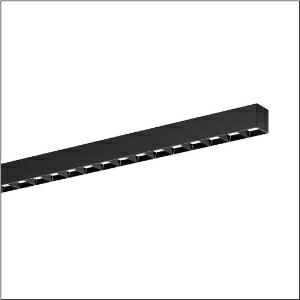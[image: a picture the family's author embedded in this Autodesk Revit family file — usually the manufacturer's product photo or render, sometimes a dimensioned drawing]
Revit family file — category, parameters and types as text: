
# Revit family: silica_21_51mx21dc3abb
name_source: partatom
category: Lighting Fixtures
units: mm (PartAtom-declared; Revit-internal decimal feet)

## family parameters
Cut with Voids When Loaded = No
Host = Face
Light Source = No
Part Type = Normal
Room Calculation Point = No
Round Connector Dimension = Use Diameter
Shared = No

## types (1)
- --- (1 x LED, 10800 lm, 69.3 W, 3000K)
    Apparent Load = 69 VA
    CIE Flux Codes = 87 99 100 100 100
    Color Rendering = 80
    Color Temperature = 3000K
    Default Elevation = 1800 mm
    Description = Silica 21, office luminaire, primary light control with darklight reflector, of PMMA, black, CAT 2 (L<= 3000cd/m²), light emission: direct distribution, primary light characteristic: symmetric, installation type: surface-mounted, LED, rated luminous flux: 10.800lm, luminous efficacy: 156lm/W, light colour: 830, colour temperature: 3000K, control gear: DALI 2, with terminal, 3+2-pole, max. 2.5mm², mains connection: 220..240V, AC, 50/60Hz, luminaire housing, of aluminium, matt jet black (RAL 9005), length: 3.004mm, width: 53mm, height: 53mm, protection rating (complete): IP20, insulation class (complete): insulation class I (protective earthing), certification: CE, permissible operating ambient temperature: 0..+35°C, standard: EN 50419, packaging unit: 1 piece
    Height = 53 mm
    Lamp = 1 x LED
    Lamp Light Flux = 10800 lm
    Lamp Power = 69.3 W
    Lamp count = 1
    Length = 3004 mm
    Luminous efficacy = 156 lm/W
    Manufacturer = Siteco
    ModVariant = No
    Model = 51MX21DC3ABB
    Mounting Place = Ceiling
    Mounting Type = Surface mounted
    Number of Poles = 1
    OnlyDefault = Yes
    Power Factor = 1
    Product Name = Silica 21
    Product group = office luminaire | ceiling mounted
    ProductGroupID = 301
    Protection Class = Protection class I
    Protection Degree = IP 20
    RLX_Detail_Level = 1
    RLX_Emergency_Light_Flux = 0 lm
    RLX_Emergency_Type = 0
    RLX_Emergency_Type_DB = No
    RlxData = <blob elided: 64637 chars, md5=dbf83905>
    Socket = socket
    Standby Power = 0 W
    System Light Flux = 10800 lm
    System Power = 69 W
    Type Comments = factory setting: luminous flux: 100 % | dim-lin: 254 | 393 mA
    Type Image = l_1335908.jpg
    URL = http://relux.com
    VarID = @adj_125387
    Voltage = 0 V
    Weight = 0.00 kg
    Width = 53 mm

## geometry (parser evidence)
native form markers: Blend x4, Sweep x10
no freeform markers — native parametric forms only
